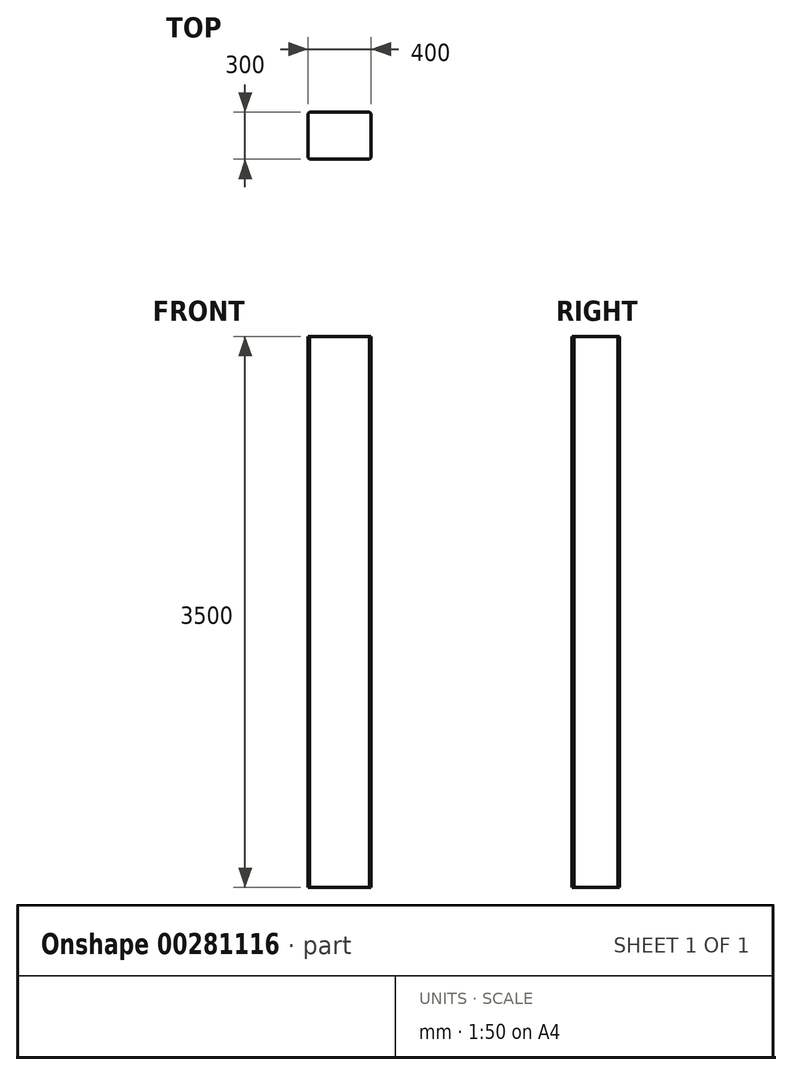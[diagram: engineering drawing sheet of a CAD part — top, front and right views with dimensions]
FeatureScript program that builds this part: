
annotation { "Feature Type Name" : "Feature", "Feature Type Description" : "" }
export const myFeature = defineFeature(function(context is Context, id is Id, definition is map)
    precondition{}
    {
        {
            var Q0;
            Q0=qCreatedBy(makeId("Top.planeOp"),FACE);
            var sketch = newSketch(context, id + "F0", { "sketchPlane" : qUnion([Q0])});
            skLineSegment(sketch, "E0.bottom", {"start": v(200, -150) * mm, "end": v(-200, -150) * mm});
            skLineSegment(sketch, "E0.top", {"start": v(200, 150) * mm, "end": v(-200, 150) * mm});
            skLineSegment(sketch, "E0.left", {"start": v(200, -150) * mm, "end": v(200, 150) * mm});
            skLineSegment(sketch, "E0.right", {"start": v(-200, -150) * mm, "end": v(-200, 150) * mm});
            skPoint(sketch, "E0.middle", {"position": v(0, 0) * mm});
            skSolve(sketch);
        }
        {
            var Q0;
            Q0 = qSketchRegion(id + "F0", true);
            extrude(context, id + "F1", {"entities" : qUnion([Q0]), "depth" : 3500 * mm});
        }
        {
            var Q0;
            Q0=makeQuery(id+"F1.opExtrude","SWEPT_EDGE",EDGE,{"disambiguationData":[OSD([sQuery(id+"F0.wireOp",EDGE,"E0.bottom"),sQuery(id+"F0.wireOp",EDGE,"E0.left")])]});
            var Q1;
            Q1=makeQuery(id+"F1.opExtrude","SWEPT_EDGE",EDGE,{"disambiguationData":[OSD([sQuery(id+"F0.wireOp",EDGE,"E0.bottom"),sQuery(id+"F0.wireOp",EDGE,"E0.right")])]});
            var Q2;
            Q2=makeQuery(id+"F1.opExtrude","SWEPT_EDGE",EDGE,{"disambiguationData":[OSD([sQuery(id+"F0.wireOp",EDGE,"E0.top"),sQuery(id+"F0.wireOp",EDGE,"E0.left")])]});
            var Q3;
            Q3=makeQuery(id+"F1.opExtrude","SWEPT_EDGE",EDGE,{"disambiguationData":[OSD([sQuery(id+"F0.wireOp",EDGE,"E0.top"),sQuery(id+"F0.wireOp",EDGE,"E0.right")])]});
            chamfer(context, id + "F2", {"entities" : qUnion([Q0, Q1, Q2, Q3]), "width" : 10 * mm, "tangentPropagation" : true});
        }
    });
